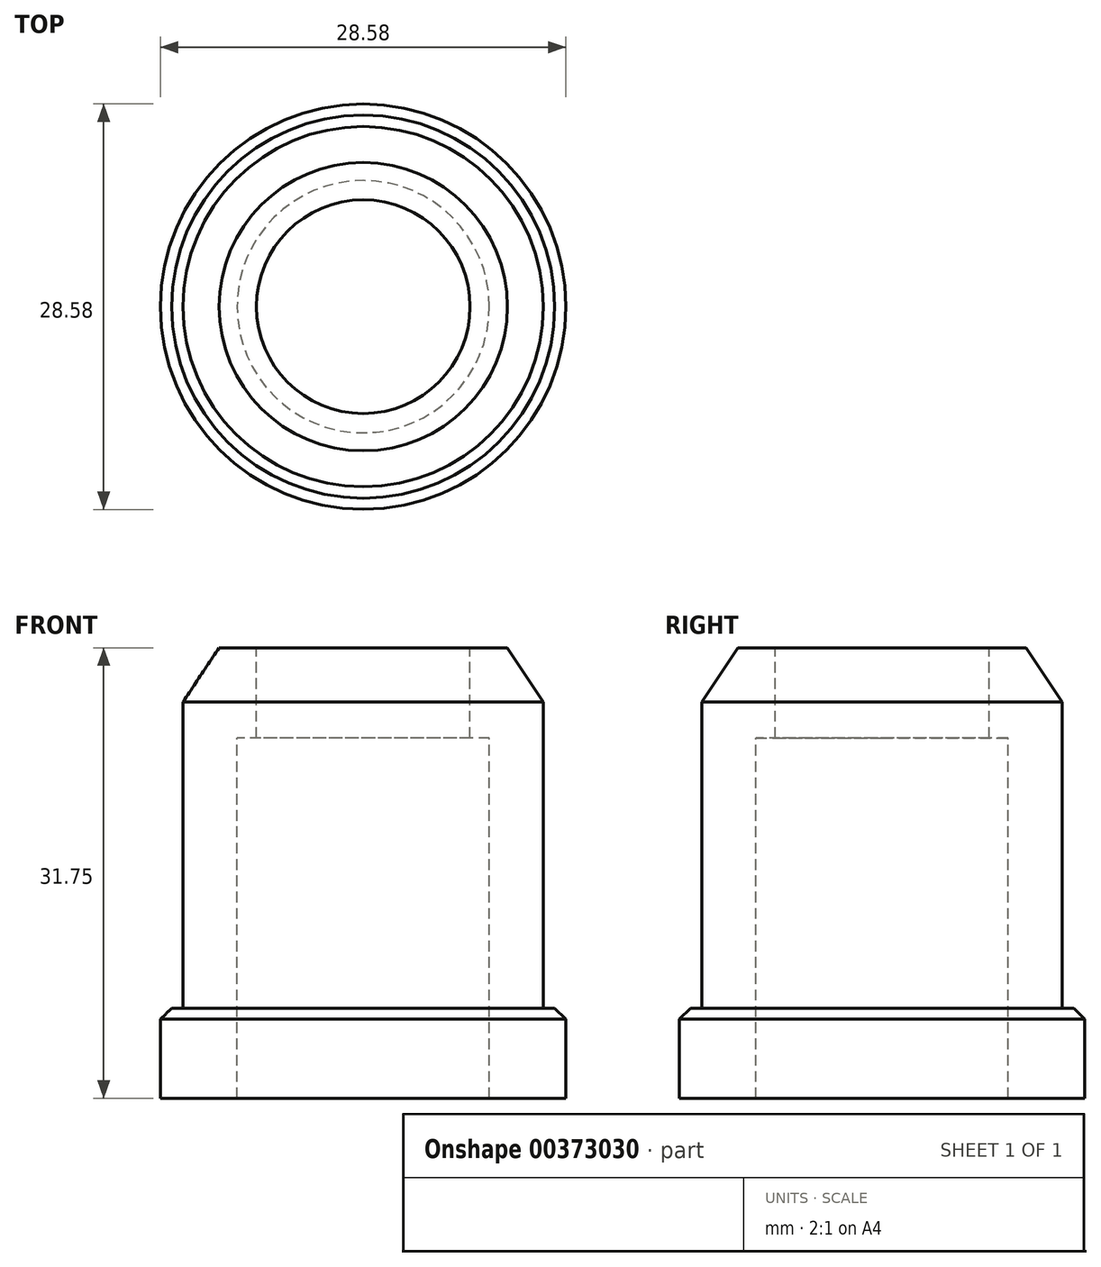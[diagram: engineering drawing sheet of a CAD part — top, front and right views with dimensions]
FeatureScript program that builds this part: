
annotation { "Feature Type Name" : "Feature", "Feature Type Description" : "" }
export const myFeature = defineFeature(function(context is Context, id is Id, definition is map)
    precondition{}
    {
        {
            var Q0;
            Q0=qCreatedBy(makeId("Front.planeOp"),FACE);
            var sketch = newSketch(context, id + "F0", { "sketchPlane" : qUnion([Q0])});
            skLineSegment(sketch, "E0", {"start": v(0, 14.66) * mm, "end": v(0, 0) * mm});
            skLineSegment(sketch, "E1", {"start": v(0, 0) * mm, "end": v(-14.29, 0) * mm});
            skLineSegment(sketch, "E2", {"start": v(-14.29, 0) * mm, "end": v(-14.29, 6.35) * mm});
            skLineSegment(sketch, "E3", {"start": v(-14.29, 6.35) * mm, "end": v(-12.7, 6.35) * mm});
            skLineSegment(sketch, "E4", {"start": v(-12.7, 6.35) * mm, "end": v(-12.7, 31.75) * mm});
            skLineSegment(sketch, "E5", {"start": v(-12.7, 31.75) * mm, "end": v(-7.53, 31.75) * mm});
            skLineSegment(sketch, "E6", {"start": v(-7.53, 31.75) * mm, "end": v(-7.53, 25.4) * mm});
            skLineSegment(sketch, "E7", {"start": v(-8.9, 0) * mm, "end": v(-8.9, 25.4) * mm});
            skLineSegment(sketch, "E8", {"start": v(-7.53, 25.4) * mm, "end": v(-8.9, 25.4) * mm});
            skSolve(sketch);
        }
        {
            var Q0;
            {var subQ0=sQuery(id+"F0.wireOp",EDGE,"E2");Q0=makeQuery(id+"F0.imprint","IMPRINT",FACE,{"disambiguationData":[TD([[makeQuery(id+"F0.imprint","IMPRINT",EDGE,{"derivedFrom":subQ0}),-1.0]])]});}
            var Q1;
            Q1=sQuery(id+"F0.wireOp",EDGE,"E0");
            revolve(context, id + "F1", {"surfaceOperationType" : NewSurfaceOperationType.NEW, "entities" : qUnion([Q0]), "axis" : qUnion([Q1]), "revolveType" : RevolveType.FULL});
        }
        {
            var Q0;
            Q0=makeQuery(id+"F1.opRevolve","SWEPT_EDGE",EDGE,{"disambiguationData":[OSD([sQuery(id+"F0.wireOp",EDGE,"E4"),sQuery(id+"F0.wireOp",EDGE,"E5")])]});
            chamfer(context, id + "F2", {"entities" : qUnion([Q0]), "chamferType" : ChamferType.TWO_OFFSETS, "width1" : 2.54 * mm, "oppositeDirection" : false, "width2" : 3.8 * mm, "tangentPropagation" : true});
        }
        {
            var Q0;
            Q0=makeQuery(id+"F1.opRevolve","SWEPT_EDGE",EDGE,{"disambiguationData":[OSD([sQuery(id+"F0.wireOp",EDGE,"E2"),sQuery(id+"F0.wireOp",EDGE,"E3")])]});
            chamfer(context, id + "F3", {"entities" : qUnion([Q0]), "width" : 0.79 * mm, "tangentPropagation" : true});
        }
    });
